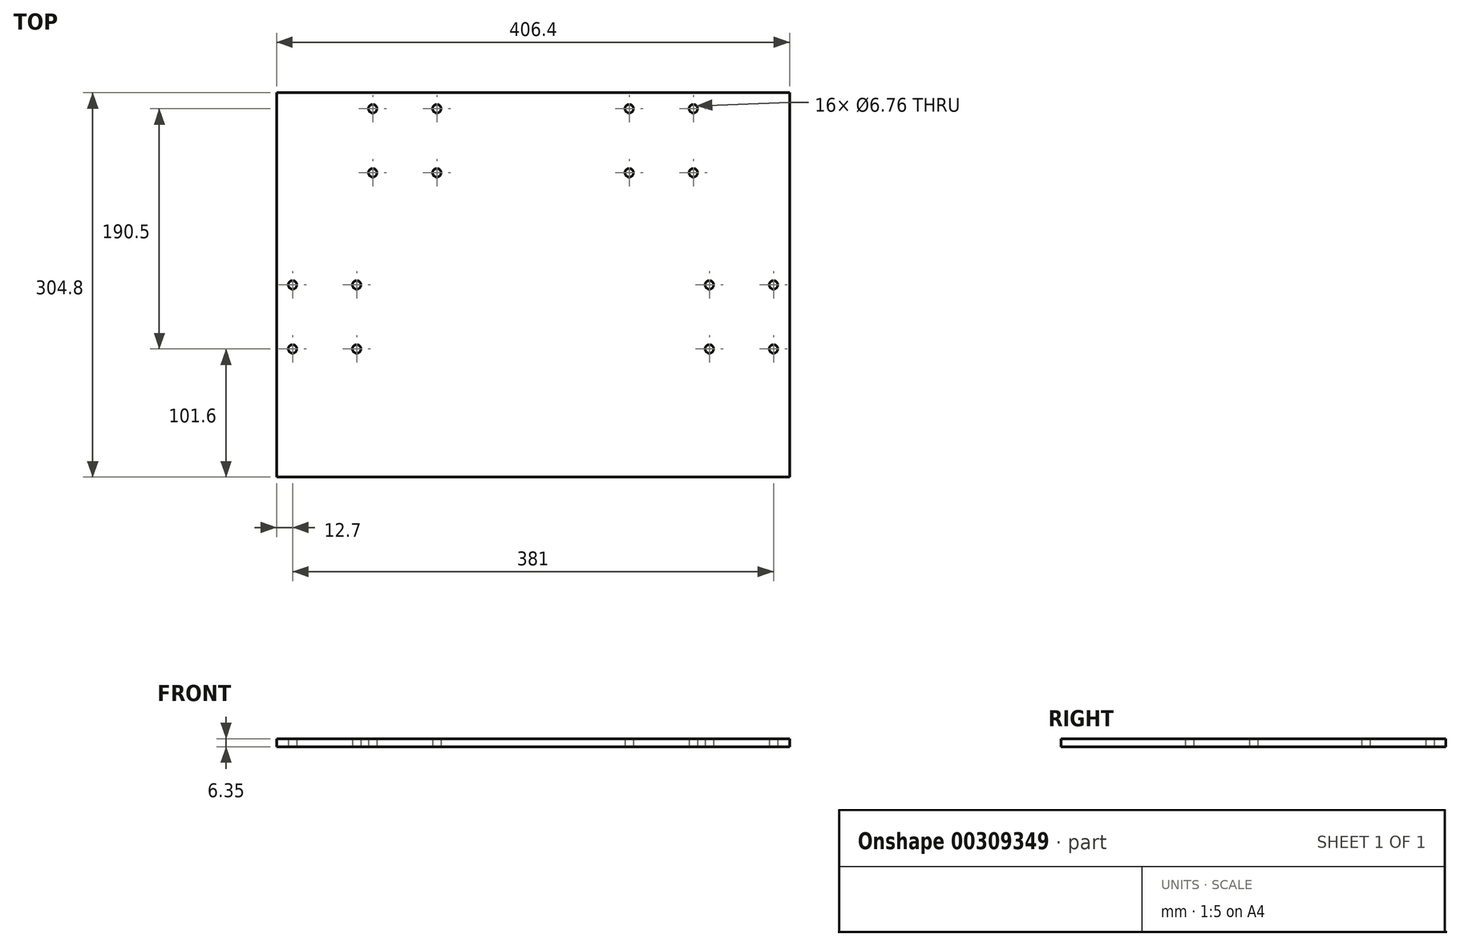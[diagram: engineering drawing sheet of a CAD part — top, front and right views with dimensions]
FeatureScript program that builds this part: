
annotation { "Feature Type Name" : "Feature", "Feature Type Description" : "" }
export const myFeature = defineFeature(function(context is Context, id is Id, definition is map)
    precondition{}
    {
        {
            var Q0;
            Q0=qCreatedBy(makeId("Top.planeOp"),FACE);
            var sketch = newSketch(context, id + "F0", { "sketchPlane" : qUnion([Q0])});
            skLineSegment(sketch, "E0.bottom", {"start": v(-203.2, 152.4) * mm, "end": v(203.2, 152.4) * mm});
            skLineSegment(sketch, "E0.top", {"start": v(-203.2, -152.4) * mm, "end": v(203.2, -152.4) * mm});
            skLineSegment(sketch, "E0.left", {"start": v(-203.2, 152.4) * mm, "end": v(-203.2, -152.4) * mm});
            skLineSegment(sketch, "E0.right", {"start": v(203.2, 152.4) * mm, "end": v(203.2, -152.4) * mm});
            skPoint(sketch, "E0.middle", {"position": v(0, 0) * mm});
            skLineSegment(sketch, "E1", {"start": v(-203.2, 152.4) * mm, "end": v(-127, 152.4) * mm});
            skLineSegment(sketch, "E2", {"start": v(-127, 152.4) * mm, "end": v(-127, 139.7) * mm});
            skLineSegment(sketch, "E3", {"start": v(-127, 139.7) * mm, "end": v(-127, 88.9) * mm});
            skLineSegment(sketch, "E4.MirrorCS", {"start": v(203.2, 152.4) * mm, "end": v(127, 152.4) * mm});
            skLineSegment(sketch, "E5.MirrorCS", {"start": v(127, 152.4) * mm, "end": v(127, 139.7) * mm});
            skLineSegment(sketch, "E6.MirrorCS", {"start": v(127, 139.7) * mm, "end": v(127, 88.9) * mm});
            skLineSegment(sketch, "E7", {"start": v(203.2, 152.4) * mm, "end": v(190.5, 152.4) * mm});
            skLineSegment(sketch, "E8", {"start": v(190.5, 152.4) * mm, "end": v(190.5, 0) * mm});
            skLineSegment(sketch, "E9", {"start": v(190.5, 0) * mm, "end": v(139.7, 0) * mm});
            skLineSegment(sketch, "E10", {"start": v(-127, 139.7) * mm, "end": v(-76.2, 139.7) * mm});
            skLineSegment(sketch, "E11", {"start": v(-127, 88.9) * mm, "end": v(-76.2, 88.9) * mm});
            skLineSegment(sketch, "E12", {"start": v(190.5, 0) * mm, "end": v(190.5, -50.8) * mm});
            skLineSegment(sketch, "E13", {"start": v(190.5, -50.8) * mm, "end": v(139.7, -50.8) * mm});
            skLineSegment(sketch, "E14.MirrorCS", {"start": v(-190.5, 152.4) * mm, "end": v(-190.5, 0) * mm});
            skLineSegment(sketch, "E15.MirrorCS", {"start": v(-190.5, 0) * mm, "end": v(-139.7, 0) * mm});
            skLineSegment(sketch, "E16.MirrorCS", {"start": v(-190.5, 0) * mm, "end": v(-190.5, -50.8) * mm});
            skLineSegment(sketch, "E17.MirrorCS", {"start": v(-190.5, -50.8) * mm, "end": v(-139.7, -50.8) * mm});
            skLineSegment(sketch, "E18.MirrorCS", {"start": v(127, 139.7) * mm, "end": v(76.2, 139.7) * mm});
            skLineSegment(sketch, "E19.MirrorCS", {"start": v(127, 88.9) * mm, "end": v(76.2, 88.9) * mm});
            skSolve(sketch);
        }
        {
            var Q0;
            Q0 = qSketchRegion(id + "F0", true);
            extrude(context, id + "F1", {"entities" : qUnion([Q0]), "depth" : 6.35 * mm});
        }
        {
            var Q0;
            Q0=sQuery(id+"F0.wireOp",VERTEX,"E3.start");
            var Q1;
            Q1=sQuery(id+"F0.wireOp",VERTEX,"E10.end");
            var Q2;
            Q2=sQuery(id+"F0.wireOp",VERTEX,"E3.end");
            var Q3;
            Q3=sQuery(id+"F0.wireOp",VERTEX,"E11.end");
            var Q4;
            Q4=sQuery(id+"F0.wireOp",VERTEX,"E18.MirrorCS.end");
            var Q5;
            Q5=sQuery(id+"F0.wireOp",VERTEX,"E6.MirrorCS.start");
            var Q6;
            Q6=sQuery(id+"F0.wireOp",VERTEX,"E19.MirrorCS.end");
            var Q7;
            Q7=sQuery(id+"F0.wireOp",VERTEX,"E19.MirrorCS.start");
            var Q8;
            Q8=sQuery(id+"F0.wireOp",VERTEX,"E9.end");
            var Q9;
            Q9=sQuery(id+"F0.wireOp",VERTEX,"E8.end");
            var Q10;
            Q10=sQuery(id+"F0.wireOp",VERTEX,"E13.end");
            var Q11;
            Q11=sQuery(id+"F0.wireOp",VERTEX,"E13.start");
            var Q12;
            Q12=sQuery(id+"F0.wireOp",VERTEX,"E15.MirrorCS.start");
            var Q13;
            Q13=sQuery(id+"F0.wireOp",VERTEX,"E15.MirrorCS.end");
            var Q14;
            Q14=sQuery(id+"F0.wireOp",VERTEX,"E17.MirrorCS.end");
            var Q15;
            Q15=sQuery(id+"F0.wireOp",VERTEX,"E16.MirrorCS.end");
            var Q16;
            Q16=makeQuery(id+"F1.opExtrude","SWEPT_BODY",BODY,{"disambiguationData":[OSD([sQuery(id+"F0.wireOp",EDGE,"E0.bottom"),sQuery(id+"F0.wireOp",EDGE,"E0.top"),sQuery(id+"F0.wireOp",EDGE,"E0.left"),sQuery(id+"F0.wireOp",EDGE,"E0.right"),sQuery(id+"F0.wireOp",EDGE,"E1"),sQuery(id+"F0.wireOp",EDGE,"E4.MirrorCS"),sQuery(id+"F0.wireOp",EDGE,"E7")])]});
            hole(context, id + "F2", {"style" : HoleStyle.SIMPLE, "endStyle" : HoleEndStyle.THROUGH, "oppositeDirection" : true, "standardTappedOrClearance" : lookupTablePath({ "standard" : "ANSI", "fit" : "Normal (ASME)", "size" : "1/4", "type" : "Clearance" }), "standardBlindInLast" : lookupTablePath({ "fit" : "Free", "standard" : "ANSI", "size" : "1/4", "type" : "Clearance" }), "holeDiameter" : 6.76 * mm, "isTappedThrough" : true, "tappedDepth" : 12.7 * mm, "tapClearance" : 3, "locations" : qUnion([Q0, Q1, Q2, Q3, Q4, Q5, Q6, Q7, Q8, Q9, Q10, Q11, Q12, Q13, Q14, Q15]), "scope" : qUnion([Q16])});
        }
    });
